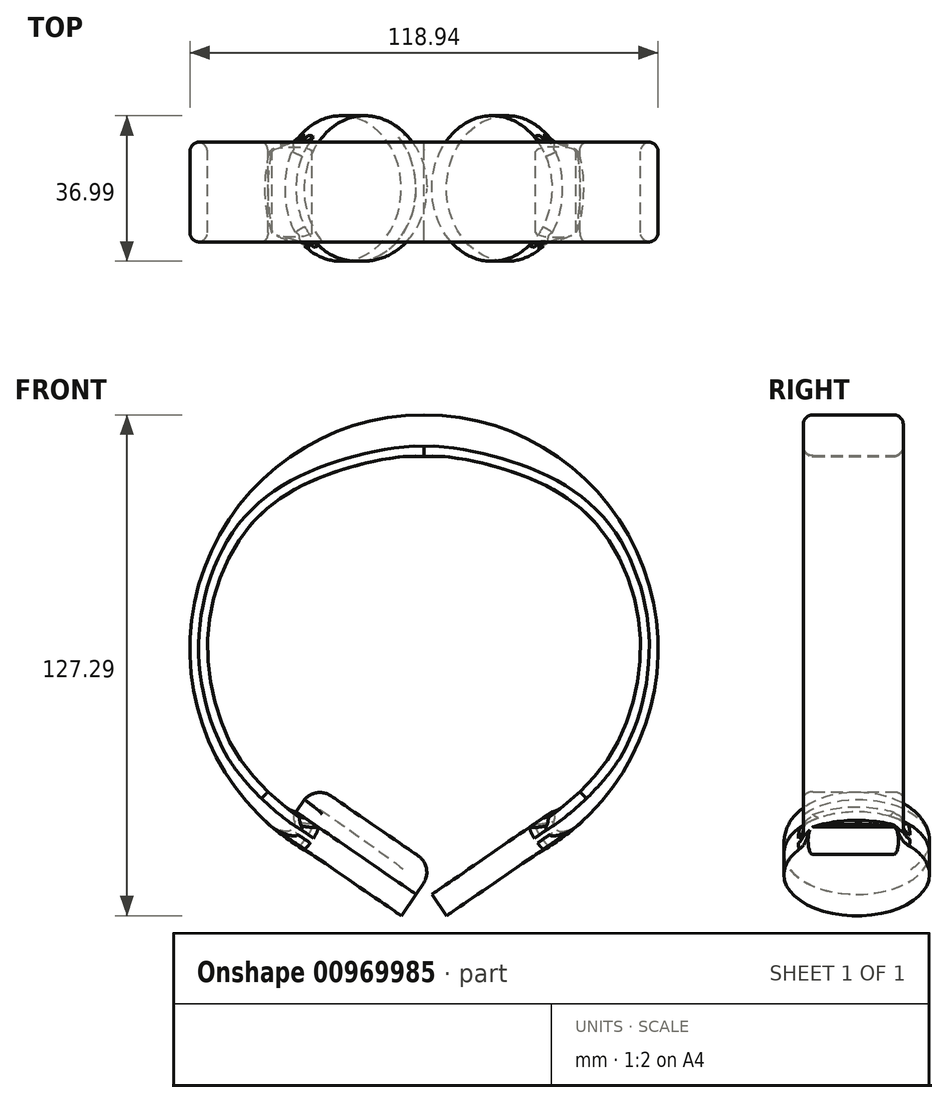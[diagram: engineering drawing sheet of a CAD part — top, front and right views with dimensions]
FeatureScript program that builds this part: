
annotation { "Feature Type Name" : "Feature", "Feature Type Description" : "" }
export const myFeature = defineFeature(function(context is Context, id is Id, definition is map)
    precondition{}
    {
        {
            var Q0;
            Q0=qCreatedBy(makeId("Right.planeOp"),FACE);
            cPlane(context, id + "F0", {"entities" : qUnion([Q0]), "cplaneType" : CPlaneType.OFFSET, "offset" : 59.69 * mm, "oppositeDirection" : true, "width" : 152.4 * mm, "height" : 152.4 * mm});
        }
        {
            var Q0;
            Q0=qCreatedBy(makeId("Front.planeOp"),FACE);
            var sketch = newSketch(context, id + "F1", { "sketchPlane" : qUnion([Q0])});
            skCircle(sketch, "E0", {"center": v(0, 0) * mm, "radius": 59.47 * mm});
            skFitSpline(sketch, "E1", {"points": [v(-39.6, -36.29) * mm, v(-49.04, -24.15) * mm, v(-55.01, 0) * mm, v(-49.81, 22.66) * mm, v(-35.56, 38.85) * mm, v(-9.35, 48.29) * mm, v(0, 48.86) * mm, v(0, 48.67) * mm], "startDerivative": vector(-69.88, 72.92) * mm, "endDerivative": vector(-4.83, -12.64) * mm});
            skLineSegment(sketch, "E2", {"start": v(0, 67.87) * mm, "end": v(0, -66.03) * mm});
            skLineSegment(sketch, "E3", {"start": v(0.03, 48.74) * mm, "end": v(0.03, 59.47) * mm});
            skFitSpline(sketch, "E4.MirrorCS", {"points": [v(39.6, -36.29) * mm, v(49.04, -24.15) * mm, v(55.01, 0) * mm, v(49.81, 22.66) * mm, v(35.56, 38.85) * mm, v(9.35, 48.29) * mm, v(0, 48.86) * mm, v(0, 48.67) * mm], "startDerivative": vector(69.88, 72.92) * mm, "endDerivative": vector(4.83, -12.64) * mm});
            skLineSegment(sketch, "E5.MirrorCS", {"start": v(39.6, -36.29) * mm, "end": v(42.95, -41.13) * mm});
            skPoint(sketch, "E6", {"position": v(-11.33, -63.99) * mm});
            skFitSpline(sketch, "E7", {"points": [v(-39.6, -36.29) * mm, v(-32.33, -42.32) * mm, v(-26.08, -45.97) * mm], "startDerivative": vector(13.7, -12.25) * mm, "endDerivative": vector(13.34, -7) * mm});
            skLineSegment(sketch, "E8", {"start": v(-26.08, -45.97) * mm, "end": v(-28.38, -52.26) * mm});
            skSolve(sketch);
        }
        {
            var Q0;
            {var subQ0=sQuery(id+"F1.wireOp",EDGE,"yAXJTIKi-DCpe-Cwv5-86Dl-3V6B5zLxSxU3");Q0=makeQuery(id+"F1.imprint","IMPRINT",FACE,{"disambiguationData":[TD([[makeQuery(id+"F1.imprint","IMPRINT",EDGE,{"derivedFrom":subQ0}),-1.0]])]});}
            var Q1;
            {var subQ0=sQuery(id+"F1.wireOp",EDGE,"E7");Q1=makeQuery(id+"F1.imprint","IMPRINT",FACE,{"disambiguationData":[TD([[makeQuery(id+"F1.imprint","IMPRINT",EDGE,{"derivedFrom":subQ0}),-1.0]])]});}
            extrude(context, id + "F2", {"entities" : qUnion([Q0, Q1]), "depth" : 25.4 * mm, "offsetDistance" : 25.4 * mm});
        }
        {
            var Q0;
            Q0=makeQuery(id+"F2.opExtrude","CAP_EDGE",EDGE,{"disambiguationData":[OSD([sQuery(id+"F1.wireOp",EDGE,"E1")])],"isStart":false});
            var Q1;
            {var subQ0=sQuery(id+"F1.wireOp",EDGE,"E0");Q1=makeQuery(id+"F2.opExtrude","CAP_EDGE",EDGE,{"disambiguationData":[OSD([subQ0]),TDD([makeQuery(id+"F1.imprint","IMPRINT",EDGE,{"disambiguationData":[TD([[makeQuery(id+"F1.imprint","INTERSECT",VERTEX,{"derivedFrom":[subQ0,sQuery(id+"F1.wireOp",EDGE,"yAXJTIKi-DCpe-Cwv5-86Dl-3V6B5zLxSxU3")]}),1.0]])],"derivedFrom":subQ0})])],"isStart":false});}
            var Q2;
            Q2=makeQuery(id+"F2.opExtrude","CAP_EDGE",EDGE,{"disambiguationData":[OSD([sQuery(id+"F1.wireOp",EDGE,"E0")])],"isStart":true});
            var Q3;
            Q3=makeQuery(id+"F2.opExtrude","CAP_EDGE",EDGE,{"disambiguationData":[OSD([sQuery(id+"F1.wireOp",EDGE,"E1")])],"isStart":true});
            var Q4;
            Q4=makeQuery(id+"F2.opExtrude","CAP_EDGE",EDGE,{"disambiguationData":[OSD([sQuery(id+"F1.wireOp",EDGE,"E7")])],"isStart":false});
            var Q5;
            Q5=makeQuery(id+"F2.opExtrude","CAP_EDGE",EDGE,{"disambiguationData":[OSD([sQuery(id+"F1.wireOp",EDGE,"E7")])],"isStart":true});
            fillet(context, id + "F3", {"entities" : qUnion([Q0, Q1, Q2, Q3, Q4, Q5]), "radius" : 2.45 * mm, "tangentPropagation" : true, "allowEdgeOverflow" : false});
        }
        {
            var Q0;
            Q0=sQuery(id+"F1.wireOp",VERTEX,"E6");
            var Q1;
            {var subQ0=sQuery(id+"F1.wireOp",EDGE,"E0");Q1=makeQuery(id+"F3.opFillet","BLEND_VERTEX",VERTEX,{"blendedFrom":[makeQuery(id+"F2.opExtrude","CAP_EDGE",EDGE,{"disambiguationData":[OSD([subQ0])],"isStart":false}),makeQuery(id+"F2.opExtrude","SWEPT_FACE",FACE,{"disambiguationData":[OSD([subQ0])]}),makeQuery(id+"F2.opExtrude","SWEPT_FACE",FACE,{"disambiguationData":[OSD([sQuery(id+"F1.wireOp",EDGE,"E8")])]})],"blendedInto":[makeQuery(id+"F2.opExtrude","SWEPT_FACE",FACE,{"disambiguationData":[OSD([subQ0])]}),makeQuery(id+"F2.opExtrude","SWEPT_FACE",FACE,{"disambiguationData":[OSD([sQuery(id+"F1.wireOp",EDGE,"E8")])]})]});}
            var Q2;
            {var subQ0=sQuery(id+"F1.wireOp",EDGE,"E0");Q2=makeQuery(id+"F3.opFillet","BLEND_VERTEX",VERTEX,{"blendedFrom":[makeQuery(id+"F2.opExtrude","CAP_EDGE",EDGE,{"disambiguationData":[OSD([subQ0])],"isStart":true}),makeQuery(id+"F2.opExtrude","SWEPT_FACE",FACE,{"disambiguationData":[OSD([subQ0])]}),makeQuery(id+"F2.opExtrude","SWEPT_FACE",FACE,{"disambiguationData":[OSD([sQuery(id+"F1.wireOp",EDGE,"E8")])]})],"blendedInto":[makeQuery(id+"F2.opExtrude","SWEPT_FACE",FACE,{"disambiguationData":[OSD([subQ0])]}),makeQuery(id+"F2.opExtrude","SWEPT_FACE",FACE,{"disambiguationData":[OSD([sQuery(id+"F1.wireOp",EDGE,"E8")])]})]});}
            cPlane(context, id + "F4", {"entities" : qUnion([Q0, Q1, Q2]), "cplaneType" : CPlaneType.THREE_POINT, "offset" : 25.4 * mm, "width" : 152.4 * mm, "height" : 152.4 * mm});
        }
        {
            var Q0;
            Q0=qCreatedBy(id+"F4.planeOp",FACE);
            var sketch = newSketch(context, id + "F5", { "sketchPlane" : qUnion([Q0])});
            skCircle(sketch, "E9", {"center": v(15.19, -11.8) * mm, "radius": 18.5 * mm});
            skSolve(sketch);
        }
        {
            var Q0;
            Q0 = qSketchRegion(id + "F5", true);
            extrude(context, id + "F6", {"entities" : qUnion([Q0]), "operationType" : NewBodyOperationType.ADD, "depth" : 6.6 * mm, "offsetDistance" : 25.4 * mm});
        }
        {
            var Q0;
            {var subQ0=sQuery(id+"F1.wireOp",EDGE,"E0");Q0=makeQuery(id+"F6.boolean.opBoolean","INTERSECT",EDGE,{"derivedFrom":[makeQuery(id+"F3.opFillet","BLEND_FACE",FACE,{"disambiguationData":[OSD([subQ0]),TDD([makeQuery(id+"F2.opExtrude","CAP_EDGE",EDGE,{"disambiguationData":[OSD([subQ0])],"isStart":true})])]}),makeQuery(id+"F6.opExtrude","SWEPT_FACE",FACE,{"disambiguationData":[OSD([sQuery(id+"F5.wireOp",EDGE,"E9")])]})]});}
            fillet(context, id + "F7", {"entities" : qUnion([Q0]), "radius" : 6.27 * mm, "tangentPropagation" : true, "allowEdgeOverflow" : false});
        }
        {
            var Q0;
            Q0=makeQuery(id+"F6.opExtrude","CAP_FACE",FACE,{"disambiguationData":[OSD([sQuery(id+"F5.wireOp",EDGE,"E9")])],"isStart":false});
            var sketch = newSketch(context, id + "F8", { "sketchPlane" : qUnion([Q0])});
            skCircle(sketch, "E10", {"center": v(15.16, -11.78) * mm, "radius": 18.5 * mm});
            skSolve(sketch);
        }
        {
            var Q0;
            Q0=makeQuery(id+"F2.opExtrude","SWEPT_BODY",BODY,{"disambiguationData":[OSD([sQuery(id+"F1.wireOp",EDGE,"E0"),sQuery(id+"F1.wireOp",EDGE,"E1"),sQuery(id+"F1.wireOp",EDGE,"E2"),sQuery(id+"F1.wireOp",EDGE,"E7"),sQuery(id+"F1.wireOp",EDGE,"E8")])]});
            var Q1;
            Q1=qCreatedBy(makeId("Right.planeOp"),FACE);
            mirror(context, id + "F9", {"operationType" : NewBodyOperationType.ADD, "entities" : qUnion([Q0]), "mirrorPlane" : qUnion([Q1])});
        }
        {
            var Q0;
            {var subQ0=sQuery(id+"F5.wireOp",EDGE,"E9");var subQ1=makeQuery(id+"F6.opExtrude","CAP_FACE",FACE,{"disambiguationData":[OSD([subQ0])],"isStart":false});var subQ2=makeQuery(id+"F6.opExtrude","SWEPT_FACE",FACE,{"disambiguationData":[OSD([subQ0])]});var subQ3=sQuery(id+"F1.wireOp",EDGE,"E7");var subQ4=makeQuery(id+"F7.opFillet","BLEND_EDGE",EDGE,{"blendedFrom":[makeQuery(id+"F6.boolean.opBoolean","INTERSECT",EDGE,{"derivedFrom":[makeQuery(id+"F3.opFillet","BLEND_FACE",FACE,{"disambiguationData":[OSD([subQ3]),TDD([makeQuery(id+"F2.opExtrude","CAP_EDGE",EDGE,{"disambiguationData":[OSD([subQ3])],"isStart":true})])]}),subQ2]}),subQ1],"blendedInto":[subQ1]});Q0=makeQuery(id+"F8.imprint","IMPRINT",FACE,{"disambiguationData":[TD([[makeQuery(id+"F8.imprint","IMPRINT",EDGE,{"derivedFrom":subQ4}),1.0]])]});}
            extrude(context, id + "F10", {"entities" : qUnion([Q0]), "operationType" : NewBodyOperationType.ADD, "depth" : 8.38 * mm, "offsetDistance" : 25.4 * mm});
        }
        {
            var Q0;
            Q0=makeQuery(id+"F10.opExtrude","CAP_EDGE",EDGE,{"disambiguationData":[OSD([sQuery(id+"F8.wireOp",EDGE,"E10")])],"isStart":false});
            fillet(context, id + "F11", {"entities" : qUnion([Q0]), "radius" : 5.08 * mm, "tangentPropagation" : true, "allowEdgeOverflow" : false});
        }
    });
